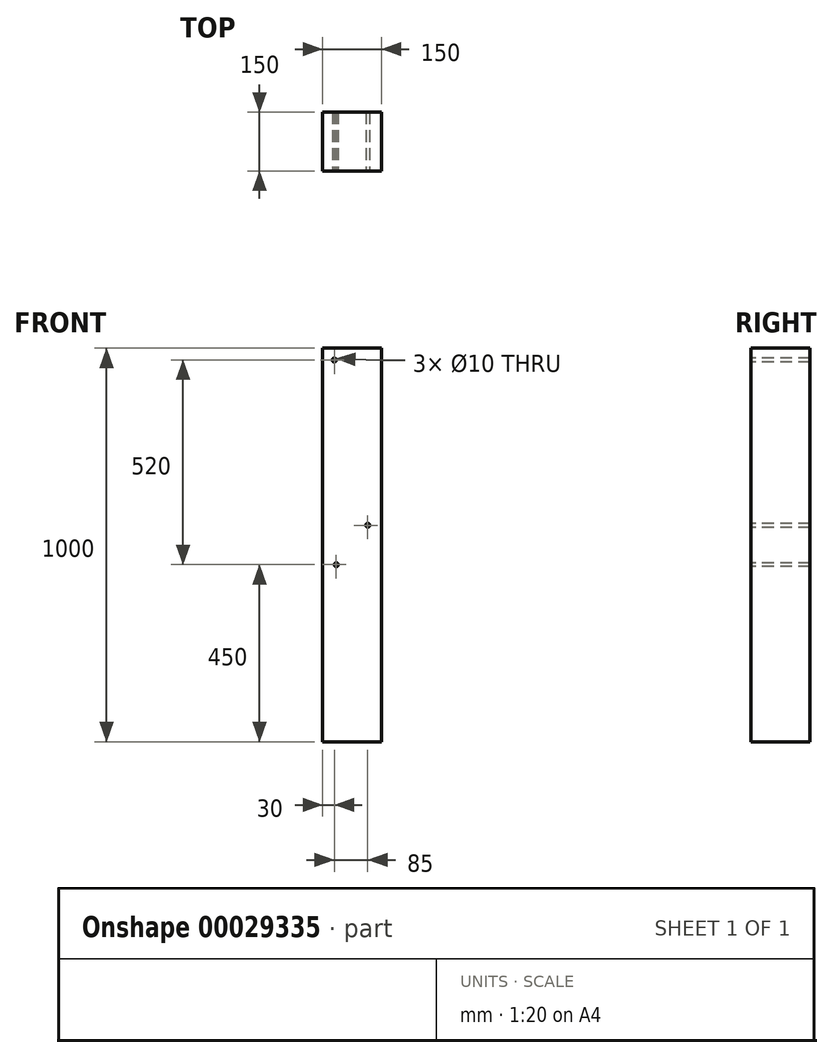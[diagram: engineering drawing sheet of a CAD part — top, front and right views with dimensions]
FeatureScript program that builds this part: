
annotation { "Feature Type Name" : "Feature", "Feature Type Description" : "" }
export const myFeature = defineFeature(function(context is Context, id is Id, definition is map)
    precondition{}
    {
        {
            var Q0;
            Q0=qCreatedBy(makeId("Front.planeOp"),FACE);
            var sketch = newSketch(context, id + "F0", { "sketchPlane" : qUnion([Q0])});
            skLineSegment(sketch, "E0.bottom", {"start": v(0, 0) * mm, "end": v(-150, 0) * mm});
            skLineSegment(sketch, "E0.top", {"start": v(0, 1000) * mm, "end": v(-150, 1000) * mm});
            skLineSegment(sketch, "E0.left", {"start": v(0, 0) * mm, "end": v(0, 1000) * mm});
            skLineSegment(sketch, "E0.right", {"start": v(-150, 0) * mm, "end": v(-150, 1000) * mm});
            skSolve(sketch);
        }
        {
            var Q0;
            Q0=makeQuery(id+"F0.imprint","IMPRINT",FACE,{"disambiguationData":[TD([[makeQuery(id+"F0.imprint","IMPRINT",EDGE,{"derivedFrom":sQuery(id+"F0.wireOp",EDGE,"E0.bottom")}),-1.0]])]});
            extrude(context, id + "F1", {"entities" : qUnion([Q0]), "oppositeDirection" : true, "depth" : 150 * mm});
        }
        {
            var Q0;
            Q0=makeQuery(id+"F1.opExtrude","CAP_FACE",FACE,{"disambiguationData":[OSD([sQuery(id+"F0.wireOp",EDGE,"E0.bottom"),sQuery(id+"F0.wireOp",EDGE,"E0.top"),sQuery(id+"F0.wireOp",EDGE,"E0.left"),sQuery(id+"F0.wireOp",EDGE,"E0.right")])],"isStart":true});
            var sketch = newSketch(context, id + "F2", { "sketchPlane" : qUnion([Q0])});
            skPoint(sketch, "E1", {"position": v(-120, 970) * mm});
            skPoint(sketch, "E2", {"position": v(-35, 550) * mm});
            skPoint(sketch, "E3", {"position": v(-115, 450) * mm});
            skSolve(sketch);
        }
        {
            var Q0;
            Q0=sQuery(id+"F2.wireOp",VERTEX,"E3");
            var Q1;
            Q1=sQuery(id+"F2.wireOp",VERTEX,"E2");
            var Q2;
            Q2=sQuery(id+"F2.wireOp",VERTEX,"E1");
            var Q3;
            Q3=makeQuery(id+"F1.opExtrude","SWEPT_BODY",BODY,{"disambiguationData":[OSD([sQuery(id+"F0.wireOp",EDGE,"E0.bottom"),sQuery(id+"F0.wireOp",EDGE,"E0.top"),sQuery(id+"F0.wireOp",EDGE,"E0.left"),sQuery(id+"F0.wireOp",EDGE,"E0.right")])]});
            hole(context, id + "F3", {"style" : HoleStyle.SIMPLE, "holeDiameter" : 10 * mm, "endStyle" : HoleEndStyle.THROUGH, "locations" : qUnion([Q0, Q1, Q2]), "scope" : qUnion([Q3]), "majorDiameter" : 5 * mm, "tappedDepth" : 12 * mm, "tapClearance" : 3});
        }
    });
